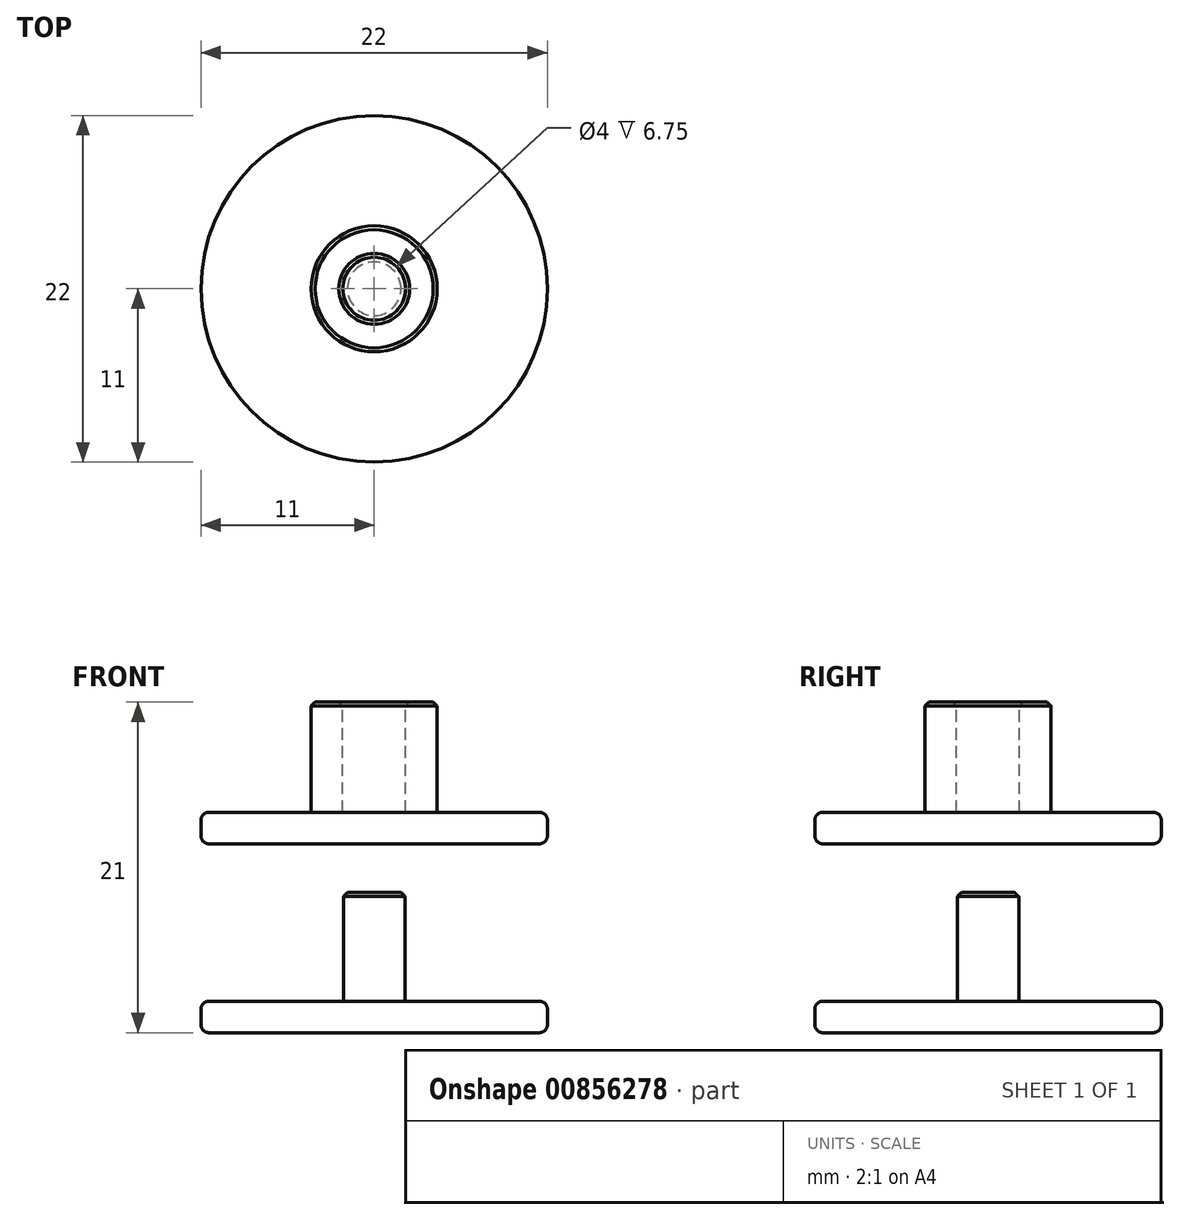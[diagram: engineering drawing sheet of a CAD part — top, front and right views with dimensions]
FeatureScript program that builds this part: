
annotation { "Feature Type Name" : "Feature", "Feature Type Description" : "" }
export const myFeature = defineFeature(function(context is Context, id is Id, definition is map)
    precondition{}
    {
        {
            var Q0;
            Q0=qCreatedBy(makeId("Top.planeOp"),FACE);
            var sketch = newSketch(context, id + "F0", { "sketchPlane" : qUnion([Q0])});
            skLineSegment(sketch, "E0", {"start": v(-11, 0) * mm, "end": v(-11, 2) * mm});
            skLineSegment(sketch, "E1", {"start": v(-11, 2) * mm, "end": v(-4, 2) * mm});
            skLineSegment(sketch, "E2", {"start": v(-2, 2) * mm, "end": v(0, 2) * mm});
            skPoint(sketch, "E3.end.orphan", {"position": v(0, 0) * mm});
            skLineSegment(sketch, "E4", {"start": v(0, 2) * mm, "end": v(0, 0) * mm});
            skLineSegment(sketch, "E5", {"start": v(-4, 2) * mm, "end": v(-4, 9) * mm});
            skLineSegment(sketch, "E6", {"start": v(-4, 9) * mm, "end": v(-2, 9) * mm});
            skLineSegment(sketch, "E7", {"start": v(-2, 9) * mm, "end": v(-2, 2) * mm});
            skLineSegment(sketch, "E8", {"start": v(-11, 0) * mm, "end": v(0, 0) * mm});
            skSolve(sketch);
        }
        {
            var Q0;
            Q0=makeQuery(id+"F0.imprint","IMPRINT",FACE,{"disambiguationData":[TD([[makeQuery(id+"F0.imprint","IMPRINT",EDGE,{"derivedFrom":sQuery(id+"F0.wireOp",EDGE,"E0")}),-1.0]])]});
            var Q1;
            Q1=sQuery(id+"F0.wireOp",EDGE,"E4");
            revolve(context, id + "F1", {"surfaceOperationType" : NewSurfaceOperationType.NEW, "entities" : qUnion([Q0]), "axis" : qUnion([Q1]), "revolveType" : RevolveType.FULL});
        }
        {
            var Q0;
            Q0=makeQuery(id+"F1.opRevolve","SWEPT_EDGE",EDGE,{"disambiguationData":[OSD([sQuery(id+"F0.wireOp",EDGE,"E0"),sQuery(id+"F0.wireOp",EDGE,"c6c6bbbc-aea4-4182-872a-2eb642a57c14")])]});
            fillet(context, id + "F2", {"entities" : qUnion([Q0]), "radius" : .5 * mm, "tangentPropagation" : true, "allowEdgeOverflow" : false});
        }
        {
            var Q0;
            Q0=qCreatedBy(makeId("Top.planeOp"),FACE);
            var sketch = newSketch(context, id + "F3", { "sketchPlane" : qUnion([Q0])});
            skLineSegment(sketch, "E9", {"start": v(-11, -12) * mm, "end": v(-11, -10) * mm});
            skLineSegment(sketch, "E10", {"start": v(-11, -10) * mm, "end": v(-1.95, -10) * mm});
            skLineSegment(sketch, "E11", {"start": v(-1.95, -10) * mm, "end": v(-1.95, -3.1) * mm});
            skLineSegment(sketch, "E12", {"start": v(-1.95, -3.1) * mm, "end": v(0, -3.1) * mm});
            skLineSegment(sketch, "E13", {"start": v(0, -3.1) * mm, "end": v(0, -10) * mm});
            skLineSegment(sketch, "E14", {"start": v(0, -10) * mm, "end": v(0, -10) * mm});
            skPoint(sketch, "E15.end.orphan", {"position": v(0, -12) * mm});
            skLineSegment(sketch, "E16", {"start": v(0, -10) * mm, "end": v(0, -12) * mm});
            skLineSegment(sketch, "E17", {"start": v(-11, -12) * mm, "end": v(0, -12) * mm});
            skSolve(sketch);
        }
        {
            var Q0;
            Q0=makeQuery(id+"F3.imprint","IMPRINT",FACE,{"disambiguationData":[TD([[makeQuery(id+"F3.imprint","IMPRINT",EDGE,{"derivedFrom":sQuery(id+"F3.wireOp",EDGE,"E9")}),-1.0]])]});
            var Q1;
            Q1=sQuery(id+"F3.wireOp",EDGE,"E13");
            revolve(context, id + "F4", {"surfaceOperationType" : NewSurfaceOperationType.NEW, "entities" : qUnion([Q0]), "axis" : qUnion([Q1]), "revolveType" : RevolveType.FULL});
        }
        {
            var Q0;
            Q0=makeQuery(id+"F4.opRevolve","SWEPT_EDGE",EDGE,{"disambiguationData":[OSD([sQuery(id+"F3.wireOp",EDGE,"E9"),sQuery(id+"F3.wireOp",EDGE,"755b04e0-a2ee-4a9a-ab7f-df39fa23db79")])]});
            fillet(context, id + "F5", {"entities" : qUnion([Q0]), "radius" : .5 * mm, "tangentPropagation" : true, "allowEdgeOverflow" : false});
        }
        {
            var Q0;
            Q0=makeQuery(id+"F4.opRevolve","SWEPT_EDGE",EDGE,{"disambiguationData":[OSD([sQuery(id+"F3.wireOp",EDGE,"E11"),sQuery(id+"F3.wireOp",EDGE,"E12")])]});
            var Q1;
            Q1=makeQuery(id+"F1.opRevolve","SWEPT_FACE",FACE,{"disambiguationData":[OSD([sQuery(id+"F0.wireOp",EDGE,"E6")])]});
            chamfer(context, id + "F6", {"entities" : qUnion([Q0, Q1]), "width" : .25 * mm, "tangentPropagation" : true});
        }
        {
            var Q0;
            Q0=qCreatedBy(makeId("Top.planeOp"),FACE);
            var sketch = newSketch(context, id + "F7", { "sketchPlane" : qUnion([Q0])});
            skLineSegment(sketch, "E18", {"start": v(0, 32.9) * mm, "end": v(0, -22.65) * mm, "construction": true});
            skLineSegment(sketch, "E19", {"start": v(-43.15, 0) * mm, "end": v(30.9, 0) * mm, "construction": true});
            skSolve(sketch);
        }
        {
            var Q0;
            Q0=makeQuery(id+"F1.opRevolve","SWEPT_BODY",BODY,{"disambiguationData":[OSD([sQuery(id+"F0.wireOp",EDGE,"E0"),sQuery(id+"F0.wireOp",EDGE,"E1"),sQuery(id+"F0.wireOp",EDGE,"E2"),sQuery(id+"F0.wireOp",EDGE,"E4"),sQuery(id+"F0.wireOp",EDGE,"c6c6bbbc-aea4-4182-872a-2eb642a57c14"),sQuery(id+"F0.wireOp",EDGE,"E5"),sQuery(id+"F0.wireOp",EDGE,"E6"),sQuery(id+"F0.wireOp",EDGE,"E7")])]});
            var Q1;
            Q1=makeQuery(id+"F4.opRevolve","SWEPT_BODY",BODY,{"disambiguationData":[OSD([sQuery(id+"F3.wireOp",EDGE,"E9"),sQuery(id+"F3.wireOp",EDGE,"E10"),sQuery(id+"F3.wireOp",EDGE,"E11"),sQuery(id+"F3.wireOp",EDGE,"E12"),sQuery(id+"F3.wireOp",EDGE,"E13"),sQuery(id+"F3.wireOp",EDGE,"E16"),sQuery(id+"F3.wireOp",EDGE,"755b04e0-a2ee-4a9a-ab7f-df39fa23db79")])]});
            var Q2;
            Q2=sQuery(id+"F7.wireOp",EDGE,"E19");
            transform(context, id + "F8", {"entities" : qUnion([Q0, Q1]), "transformType" : TransformType.ROTATION, "transformAxis" : qUnion([Q2]), "angle" : 90 * degree, "makeCopy" : false});
        }
    });
